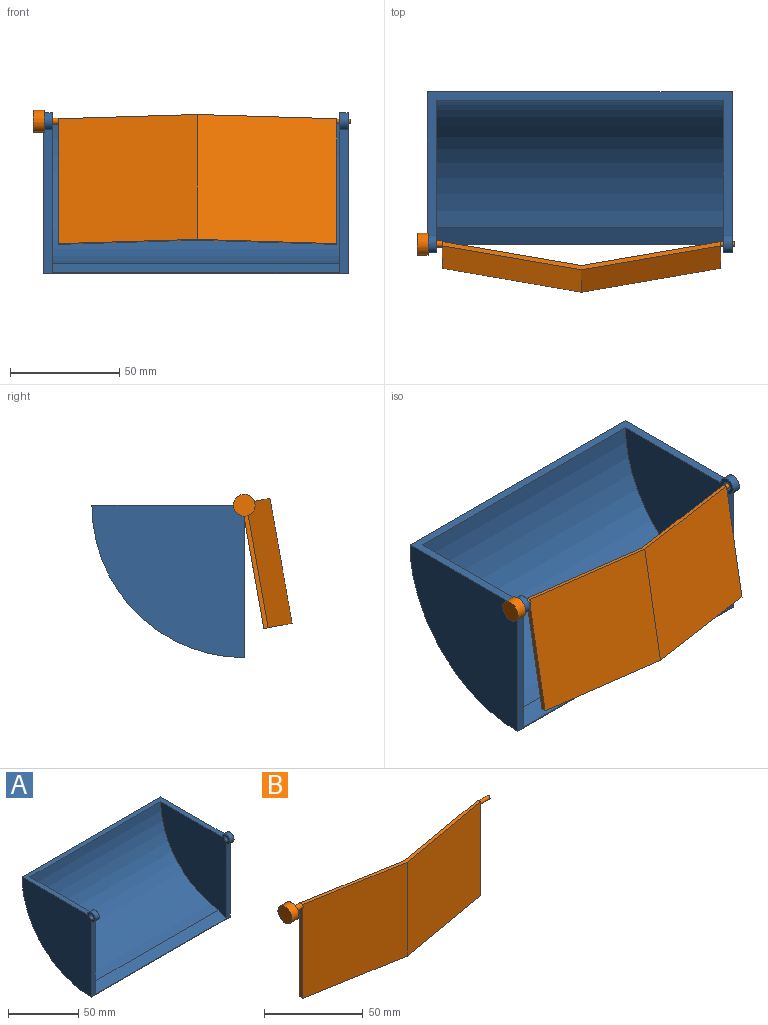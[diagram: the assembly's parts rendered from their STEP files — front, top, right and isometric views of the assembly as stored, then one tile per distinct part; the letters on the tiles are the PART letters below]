
ASSEMBLY  parts=2 mates=1
PART A: 13 faces, bbox 139.7x73.9x73.9 mm
  f0: cylinder r=69.85mm len=139.7mm, axis (1,0,0), area 15327.9mm2, adj f1,f4,f5,f9
  f1: plane 73.85x73.85mm, normal (-1,0,0), area 3857.1mm2, adj f0,f4,f5,f7,f8
  f2: plane 73.39x69.85mm, normal (1,0,0), area 3443.6mm2, adj f3,f4,f5,f6,f7,f8
  f3: cylinder r=65.85mm len=131.7mm, axis (1,0,0), area 12627.2mm2, adj f2,f5,f6,f10
  f4: plane 139.7x65.85mm, normal (0,-1,0), area 587.3mm2, adj f0,f1,f2,f6,f7,f9,f10,f11
  f5: plane 139.7x65.85mm, normal (0,0,1), area 1053.6mm2, adj f0,f1,f2,f3,f7,f9,f10,f11
  f6: plane 131.7x7.54mm, normal (0,-0.47,0.88), area 1122.7mm2, adj f2,f3,f4,f10
  f7: cylinder r=4mm len=8mm, axis (-1,0,0), area 75.4mm2, adj f1,f2,f4,f5
  f8: cylinder r=2mm len=4mm, axis (-1,0,0), area 50.3mm2, adj f1,f2
  f9: plane 73.85x73.85mm, normal (1,0,0), area 3857.1mm2, adj f0,f4,f5,f11,f12
  f10: plane 73.39x69.85mm, normal (-1,0,0), area 3443.6mm2, adj f3,f4,f5,f6,f11,f12
  f11: cylinder r=4mm len=8mm, axis (1,0,0), area 75.4mm2, adj f4,f5,f9,f10
  f12: cylinder r=2mm len=4mm, axis (1,0,0), area 50.3mm2, adj f9,f10
PART B: 17 faces, bbox 145.7x17.2x62.2 mm
  f0: plane 56.03x2mm, normal (-1,0,0), area 111.5mm2, adj f1,f2,f3,f13
  f1: plane 63.85x58.15mm, normal (0.17,0.99,0), area 3769.1mm2, adj f0,f3,f4,f10,f12
  f2: plane 63.85x58.15mm, normal (-0.17,-0.99,0), area 3769.1mm2, adj f0,f3,f4,f11,f12
  f3: plane 127.7x13.15mm, normal (0,0,-1), area 255.4mm2, adj f0,f1,f2,f9,f10,f11
  f4: plane 127.7x13.15mm, normal (0,0,1), area 255.4mm2, adj f1,f2,f7,f8,f10,f11,f12
  f5: cylinder r=1mm len=6.5mm, axis (1,0,0), area 40.8mm2, adj f6,f7,f8,f9
  f6: plane 2x2mm, normal (1,0,0), area 3.1mm2, adj f5
  f7: plane 1x1mm, normal (1,0,0), area 0.2mm2, adj f4,f5,f11
  f8: plane 1x1mm, normal (1,0,0), area 0.2mm2, adj f4,f5,f10
  f9: plane 57.15x2mm, normal (1,0,0), area 112.7mm2, adj f3,f5,f10,f11
  f10: plane 63.85x58.15mm, normal (-0.17,0.99,0), area 3769.1mm2, adj f1,f3,f4,f8,f9
  f11: plane 63.85x58.15mm, normal (0.17,-0.99,0), area 3769.1mm2, adj f2,f3,f4,f7,f9
  f12: plane 3x2.62mm, normal (1,0,0), area 2.3mm2, adj f1,f2,f4,f13
  f13: cylinder r=1.5mm len=6.5mm, axis (-1,0,0), area 61.3mm2, adj f0,f12,f16
  f14: plane 10x10mm, normal (-1,0,0), area 78.5mm2, adj f15
  f15: cylinder r=5mm len=10mm, axis (1,0,0), area 157.1mm2, adj f14,f16
  f16: plane 10x10mm, normal (1,0,0), area 71.5mm2, adj f13,f15
PLACE A t=(-34.05,25.92,-18.71)mm fixed
PLACE B rot(axis=(-1,0,0),10.1deg) t=(-33.3,24.85,-30.91)mm
MATE revolute A.f7 <-> B.f15  axis (1,0,0) through (103.65,-43.93,-18.71)mm
